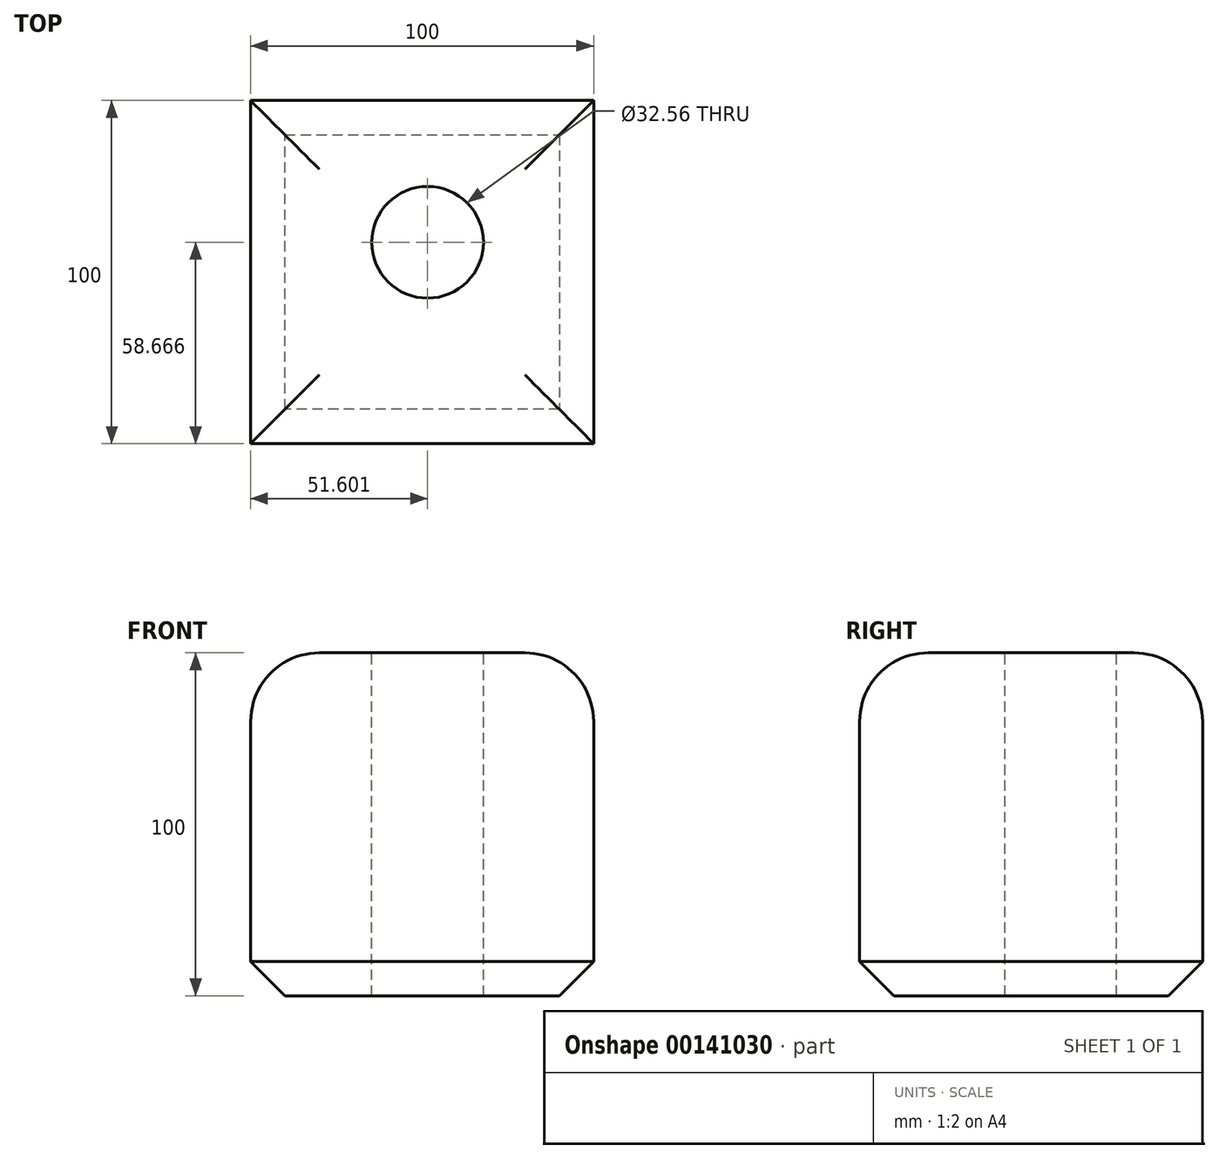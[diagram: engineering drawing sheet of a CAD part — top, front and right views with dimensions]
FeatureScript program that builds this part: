
annotation { "Feature Type Name" : "Feature", "Feature Type Description" : "" }
export const myFeature = defineFeature(function(context is Context, id is Id, definition is map)
    precondition{}
    {
        {
            var Q0;
            Q0=qCreatedBy(makeId("Top.planeOp"),FACE);
            var sketch = newSketch(context, id + "F0", { "sketchPlane" : qUnion([Q0])});
            skLineSegment(sketch, "E0.bottom", {"start": v(-46.17, 55.87) * mm, "end": v(53.83, 55.87) * mm});
            skLineSegment(sketch, "E0.top", {"start": v(-46.17, -44.13) * mm, "end": v(53.83, -44.13) * mm});
            skLineSegment(sketch, "E0.left", {"start": v(-46.17, 55.87) * mm, "end": v(-46.17, -44.13) * mm});
            skLineSegment(sketch, "E0.right", {"start": v(53.83, 55.87) * mm, "end": v(53.83, -44.13) * mm});
            skSolve(sketch);
        }
        {
            var Q0;
            Q0 = qSketchRegion(id + "F0", true);
            extrude(context, id + "F1", {"entities" : qUnion([Q0]), "depth" : 100 * mm});
        }
        {
            var Q0;
            Q0=makeQuery(id+"F1.opExtrude","CAP_EDGE",EDGE,{"disambiguationData":[OSD([sQuery(id+"F0.wireOp",EDGE,"E0.left")])],"isStart":false});
            var Q1;
            Q1=makeQuery(id+"F1.opExtrude","CAP_EDGE",EDGE,{"disambiguationData":[OSD([sQuery(id+"F0.wireOp",EDGE,"E0.top")])],"isStart":false});
            var Q2;
            Q2=makeQuery(id+"F1.opExtrude","CAP_EDGE",EDGE,{"disambiguationData":[OSD([sQuery(id+"F0.wireOp",EDGE,"E0.bottom")])],"isStart":false});
            var Q3;
            Q3=makeQuery(id+"F1.opExtrude","CAP_EDGE",EDGE,{"disambiguationData":[OSD([sQuery(id+"F0.wireOp",EDGE,"E0.right")])],"isStart":false});
            fillet(context, id + "F2", {"entities" : qUnion([Q0, Q1, Q2, Q3]), "radius" : 20 * mm, "tangentPropagation" : true, "allowEdgeOverflow" : false});
        }
        {
            var Q0;
            Q0=makeQuery(id+"F1.opExtrude","CAP_EDGE",EDGE,{"disambiguationData":[OSD([sQuery(id+"F0.wireOp",EDGE,"E0.top")])],"isStart":true});
            var Q1;
            Q1=makeQuery(id+"F1.opExtrude","CAP_EDGE",EDGE,{"disambiguationData":[OSD([sQuery(id+"F0.wireOp",EDGE,"E0.right")])],"isStart":true});
            var Q2;
            Q2=makeQuery(id+"F1.opExtrude","CAP_EDGE",EDGE,{"disambiguationData":[OSD([sQuery(id+"F0.wireOp",EDGE,"E0.bottom")])],"isStart":true});
            var Q3;
            Q3=makeQuery(id+"F1.opExtrude","CAP_EDGE",EDGE,{"disambiguationData":[OSD([sQuery(id+"F0.wireOp",EDGE,"E0.left")])],"isStart":true});
            chamfer(context, id + "F3", {"entities" : qUnion([Q0, Q1, Q2, Q3]), "width" : 10 * mm, "tangentPropagation" : true});
        }
        {
            var Q0;
            Q0=makeQuery(id+"F1.opExtrude","CAP_FACE",FACE,{"disambiguationData":[OSD([sQuery(id+"F0.wireOp",EDGE,"E0.bottom"),sQuery(id+"F0.wireOp",EDGE,"E0.top"),sQuery(id+"F0.wireOp",EDGE,"E0.left"),sQuery(id+"F0.wireOp",EDGE,"E0.right")])],"isStart":false});
            var sketch = newSketch(context, id + "F4", { "sketchPlane" : qUnion([Q0])});
            skCircle(sketch, "E1", {"center": v(5.43, 14.54) * mm, "radius": 16.28 * mm});
            skSolve(sketch);
        }
        {
            var Q0;
            Q0=makeQuery(id+"F4.imprint","IMPRINT",FACE,{"disambiguationData":[TD([[makeQuery(id+"F4.imprint","IMPRINT",EDGE,{"derivedFrom":sQuery(id+"F4.wireOp",EDGE,"E1")}),1.0]])]});
            extrude(context, id + "F5", {"entities" : qUnion([Q0]), "operationType" : NewBodyOperationType.REMOVE, "oppositeDirection" : true, "depth" : 173.82 * mm});
        }
    });
